# Revit family: Deck Panel Ended 800 Deep 750 High
name_source: partatom
category: Furniture
units: mm (PartAtom-declared; Revit-internal decimal feet)

## family parameters
Always vertical = Yes
Cut with Voids When Loaded = No
OmniClass Number = 23.40.20.00
OmniClass Title = General Furniture and Specialties
Room Calculation Point = No
Shared = No
Work Plane-Based = No

## types (5) — shared parameters
Assembly Code = E2020200
Foot = Gresham - Black Plastic
Manufacturer = Gresham Office Furniture
Modesty Panel = Gresham - Grey MFC
Range = DECK
Side Panels = Gresham - Grey MFC
URL = www.gof.co.uk

## per-type parameters (varying)
| type | Product Code | Table Top | Width |
| 1400 x 800 | DCTM14 | Gresham - White MFC | 1400 mm  [stored 4.59318 ft] |
| 1600 x 800 | DCTM16 | Gresham - White MFC | 1600 mm  [stored 5.24934 ft] |
| 1800 x 800 | DCTM18 | Gresham - White MFC | 1800 mm  [stored 5.90551 ft] |
| 2000 x 800 | DCTM20 | Gresham - White MFC | 2000 mm  [stored 6.56168 ft] |
| 2200 x 800 | DCTM22 | Filafo Dial Florenzi | 2200 mm  [stored 7.21785 ft] |

note: [stored X ft] marks values corroborated as IEEE doubles in the binary element streams (Revit-internal decimal feet)

## geometry (parser evidence)
native form markers: Sweep x2
no freeform markers — native parametric forms only
